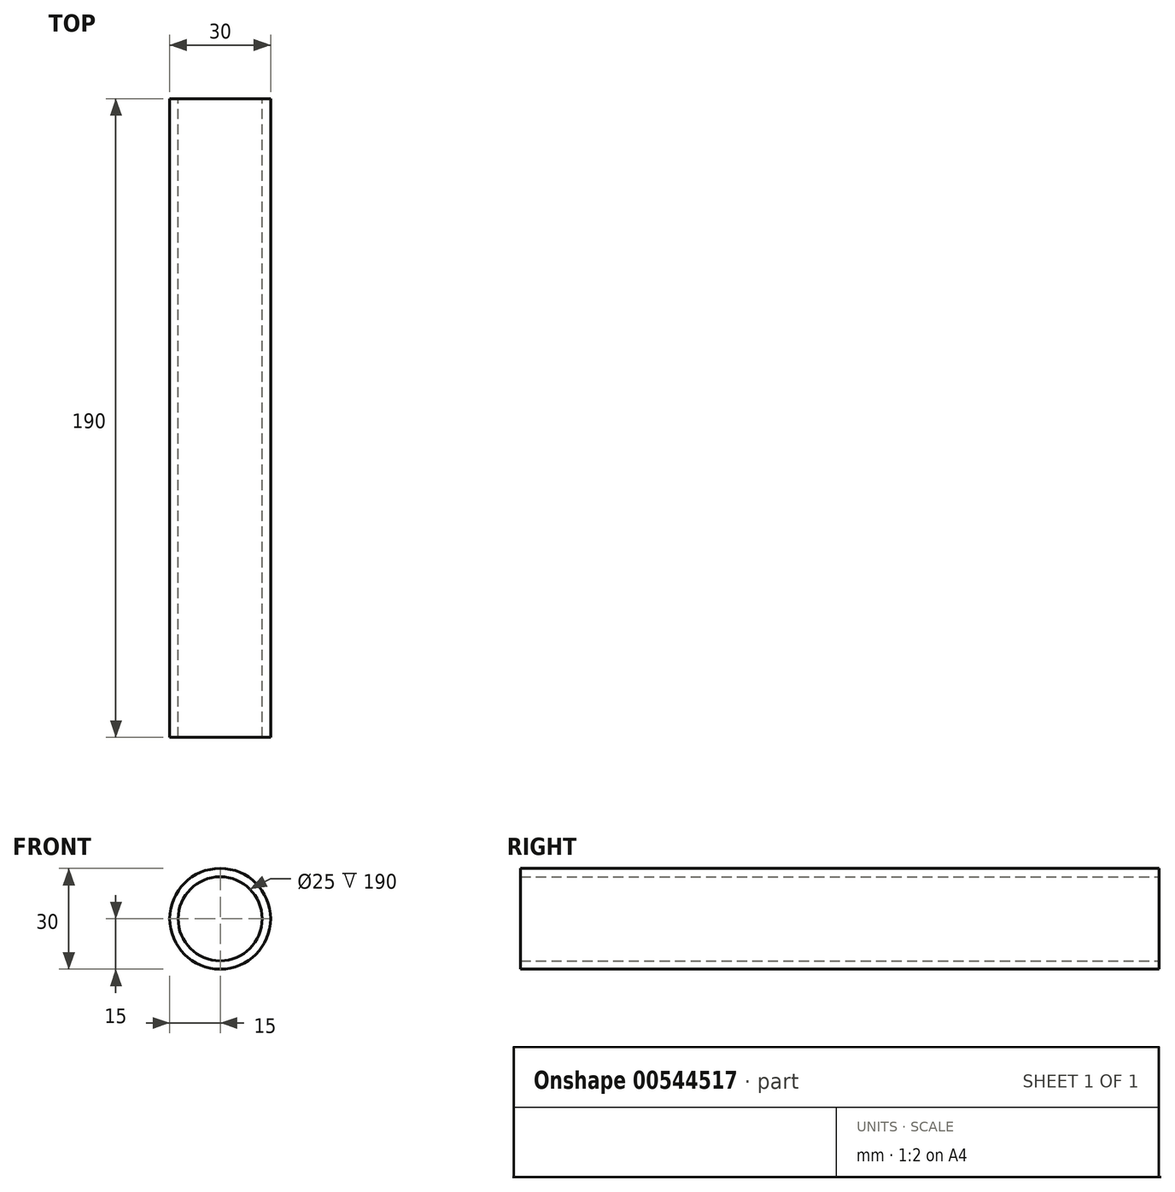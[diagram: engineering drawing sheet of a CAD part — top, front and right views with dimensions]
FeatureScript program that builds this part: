
annotation { "Feature Type Name" : "Feature", "Feature Type Description" : "" }
export const myFeature = defineFeature(function(context is Context, id is Id, definition is map)
    precondition{}
    {
        {
            var Q0;
            Q0=qCreatedBy(makeId("Front.planeOp"),FACE);
            var sketch = newSketch(context, id + "F0", { "sketchPlane" : qUnion([Q0])});
            skCircle(sketch, "E0", {"center": v(0, 0) * mm, "radius": 15 * mm});
            skCircle(sketch, "E1", {"center": v(0, 0) * mm, "radius": 12.5 * mm});
            skSolve(sketch);
        }
        {
            var Q0;
            Q0=makeQuery(id+"F0.imprint","IMPRINT",FACE,{"disambiguationData":[TD([[makeQuery(id+"F0.imprint","IMPRINT",EDGE,{"derivedFrom":sQuery(id+"F0.wireOp",EDGE,"E0")}),1.0]])]});
            extrude(context, id + "F1", {"entities" : qUnion([Q0]), "depth" : 190 * mm, "offsetDistance" : 25 * mm});
        }
    });
